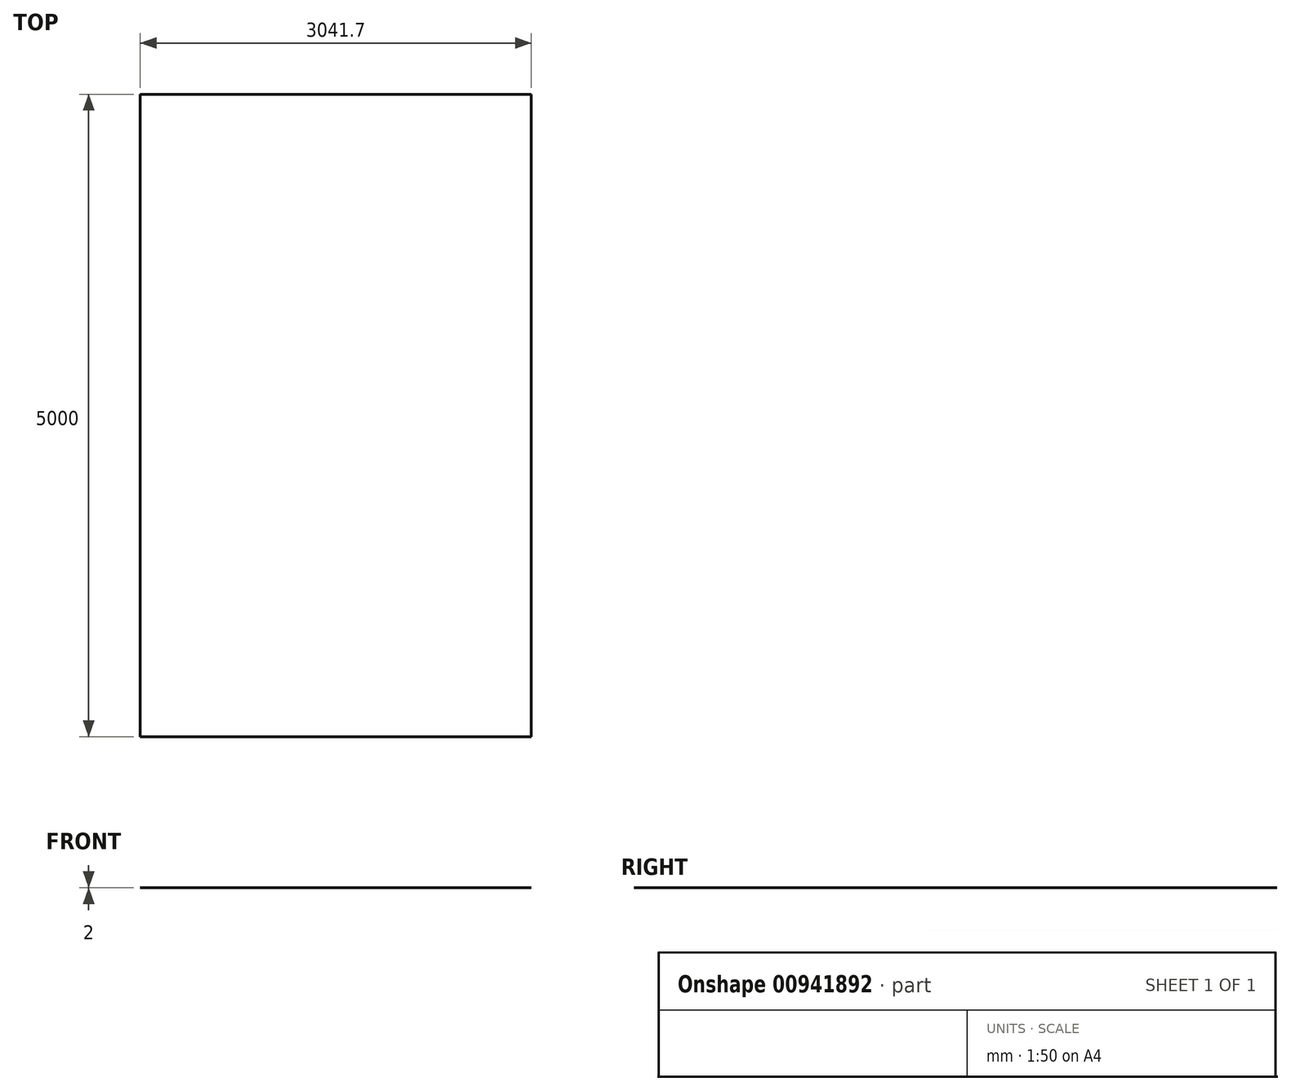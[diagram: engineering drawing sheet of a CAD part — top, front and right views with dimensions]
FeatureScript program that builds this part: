
annotation { "Feature Type Name" : "Feature", "Feature Type Description" : "" }
export const myFeature = defineFeature(function(context is Context, id is Id, definition is map)
    precondition{}
    {
        {
            var Q0;
            Q0=qCreatedBy(makeId("Top.planeOp"),FACE);
            var sketch = newSketch(context, id + "F0", { "sketchPlane" : qUnion([Q0])});
            skLineSegment(sketch, "E0.bottom", {"start": v(0, 0) * mm, "end": v(3041.7, 0) * mm});
            skLineSegment(sketch, "E0.top", {"start": v(0, 5000) * mm, "end": v(3041.7, 5000) * mm});
            skLineSegment(sketch, "E0.left", {"start": v(0, 0) * mm, "end": v(0, 5000) * mm});
            skLineSegment(sketch, "E0.right", {"start": v(3041.7, 0) * mm, "end": v(3041.7, 5000) * mm});
            skSolve(sketch);
        }
        {
            var Q0;
            Q0=makeQuery(id+"F0.imprint","IMPRINT",FACE,{"disambiguationData":[TD([[makeQuery(id+"F0.imprint","IMPRINT",EDGE,{"derivedFrom":sQuery(id+"F0.wireOp",EDGE,"E0.bottom")}),1.0]])]});
            extrude(context, id + "F1", {"entities" : qUnion([Q0]), "depth" : 2 * mm, "offsetDistance" : 25 * mm});
        }
    });
